# Revit family: Toilet-American_Standard-Right_Width-3641.001
name_source: partatom
category: Plumbing Fixtures
revit_build: Autodesk Revit 2014 (Build: 20130308_1515(x64)
units: mm (PartAtom-declared; Revit-internal decimal feet)

## types (1)
- 3641.001
    ADA Compliant = Yes
    Assembly Code = D2010110
    Bowl Shape = Elongated
    CW Connection = Yes
    CWFU = 10
    Cold Water Connection Diameter = 1"
    Cold Water Connection Radius = 1/2"
    Description = 3641.001-American Standard-Right Width FloWise Elongated Right Height Flushometer Toilet - Top spud.
    Flow Rate = 6.0 Lpf/1.3 gpf
    HW Connection = No
    HWFU = 0
    Height = 17 1/8"
    Installation Type = Deck Mounted
    Length = 28 1/4"
    Manufacturer = American Standard
    Material = Vitreous China-American Standard-020
    Model = 3641.001
    Price = Prices may vary. Please consult Manufacturer Representative for most up-to-date price list.
    Product Documentation Link = http://www.americanstandard.ca
    Product Page URL = http://www.americanstandard.ca
    Revised Date = 06/16/2015
    URL = http://www.americanstandard.ca
    Vent Connection = No
    WFU = 10
    Warranty Information = 1 Year Limited
    Waste Connection = Yes
    Waste Connection Diameter = 2"
    Waste Connection Radius = 1"
    Width = 17"

## geometry (parser evidence)
native form markers: Sweep x1
no freeform markers — native parametric forms only
